# Revit family: Fix wallmount cabinets Legrand Linkeo with removable side panel
name_source: partatom
category: Equipement spécialisé
units: mm (PartAtom-declared; Revit-internal decimal feet)

## family parameters
Basée sur le plan de construction = Non
Cote de connecteur circulaire = Utiliser le diamètre
Couper avec des vides une fois chargée = Non
Numéro OmniClass = 23.80.30.11.17
Partagée = Oui
Point de calcul de pièce = Non
Titre OmniClass = Distribution Boards and Control Panels
Toujours verticalement = Oui
Type d'élément = Normal

## types (12) — shared parameters
Application class = Network cabinets
Avec porte frontale = Oui
Color = IDS_GRIS
Degree of protection IK = IK08
Degree of protection IP = IP20
Demountable = Oui
E-catalogue link = https://www.legrand.fr
Function = Fix wallmount cabinets Linkeo Legrand
Material = Steel
Model = With permanent frame
Modular spacing = IDS_482.6_MM_19_POUCES
Mounting level = Front side
Number of doors = 1
RAL Number = 7016
Rack location = 40 mm  [stored 0.131234 ft]
Thickness (mm) = 1.5 mm  [stored 0.00492126 ft]
Type of profile rail = L-shaped
Type of surface = Powder coating
Type of ventilation = Passive
Usable width (mm) = 527 mm  [stored 1.729 ft]
Width (mm) = 608 mm  [stored 1.99475 ft]
With earthing = Oui
With roof plate = Oui
With sidewall = Oui
X fixation = 400 mm  [stored 1.31234 ft]
zero-valued in all types: Elévation par défaut

## per-type parameters (varying)
| type | Depth (mm) | EAN | Height (mm) | Legrand part number | Max load capacity | Number of height units | Usable height (mm) | Y fixation |
| Fix wallmount cabinet Legrand Linkeo 12U W600 D450 Flatpack 646252.rfa | 458 mm | 3414970968036 | 625 mm  [stored 2.05052 ft] | 646252 | 36 | 12 | 555 mm  [stored 1.82087 ft] | 419 mm |
| Fix wallmount cabinet Legrand Linkeo 12U W600 D600 Flatpack 646262.rfa | 608 mm  [stored 1.99475 ft] | 3414970968098 | 625 mm  [stored 2.05052 ft] | 646262 | 36 | 12 | 555 mm  [stored 1.82087 ft] | 419 mm |
| Fix wallmount cabinet Legrand Linkeo 15U W600 D450 Flatpack 646253.rfa | 458 mm | 3414970968043 | 759 mm  [stored 2.49016 ft] | 646253 | 45 | 15 | 688 mm  [stored 2.25722 ft] | 552 mm  [stored 1.81102 ft] |
| Fix wallmount cabinet Legrand Linkeo 15U W600 D600 Flatpack 646263.rfa | 608 mm  [stored 1.99475 ft] | 3414970968104 | 759 mm  [stored 2.49016 ft] | 646263 | 45 | 15 | 688 mm  [stored 2.25722 ft] | 552 mm  [stored 1.81102 ft] |
| Fix wallmount cabinet Legrand Linkeo 18U W600 D450 Flatpack 646254.rfa | 458 mm | 3414970968050 | 892 mm  [stored 2.92651 ft] | 646254 | 54 | 18 | 821 mm  [stored 2.69357 ft] | 685 mm |
| Fix wallmount cabinet Legrand Linkeo 18U W600 D600 Flatpack 646264.rfa | 608 mm  [stored 1.99475 ft] | 3414970968111 | 892 mm  [stored 2.92651 ft] | 646264 | 54 | 18 | 821 mm  [stored 2.69357 ft] | 685 mm |
| Fix wallmount cabinet Legrand Linkeo 21U W600 D450 Flatpack 646255.rfa | 458 mm | 3414970968067 | 1025 mm  [stored 3.36286 ft] | 646255 | 63 | 21 | 955 mm  [stored 3.1332 ft] | 819 mm  [stored 2.68701 ft] |
| Fix wallmount cabinet Legrand Linkeo 21U W600 D600 Flatpack 646265.rfa | 608 mm  [stored 1.99475 ft] | 3414970968128 | 1025 mm  [stored 3.36286 ft] | 646265 | 63 | 21 | 955 mm  [stored 3.1332 ft] | 819 mm  [stored 2.68701 ft] |
| Fix wallmount cabinet Legrand Linkeo 6U W600 D450 Flatpack 646250.rfa | 458 mm | 3414970968012 | 359 mm  [stored 1.17782 ft] | 646250 | 18 | 6 | 288 mm  [stored 0.944882 ft] | 152 mm  [stored 0.498688 ft] |
| Fix wallmount cabinet Legrand Linkeo 6U W600 D600 Flatpack 646260.rfa | 608 mm  [stored 1.99475 ft] | 3414970968074 | 359 mm  [stored 1.17782 ft] | 646260 | 18 | 6 | 288 mm  [stored 0.944882 ft] | 152 mm  [stored 0.498688 ft] |
| Fix wallmount cabinet Legrand Linkeo 9U W600 D450 Flatpack 646251.rfa | 458 mm | 3414970968029 | 492 mm  [stored 1.61417 ft] | 646251 | 27 | 9 | 422 mm  [stored 1.38451 ft] | 286 mm |
| Fix wallmount cabinet Legrand Linkeo 9U W600 D600 Flatpack 646261.rfa | 608 mm  [stored 1.99475 ft] | 3414970968081 | 492 mm  [stored 1.61417 ft] | 646261 | 27 | 9 | 422 mm  [stored 1.38451 ft] | 286 mm |

note: column(s) folded — value = type name in every type: BIM wording

note: [stored X ft] marks values corroborated as IEEE doubles in the binary element streams (Revit-internal decimal feet)
